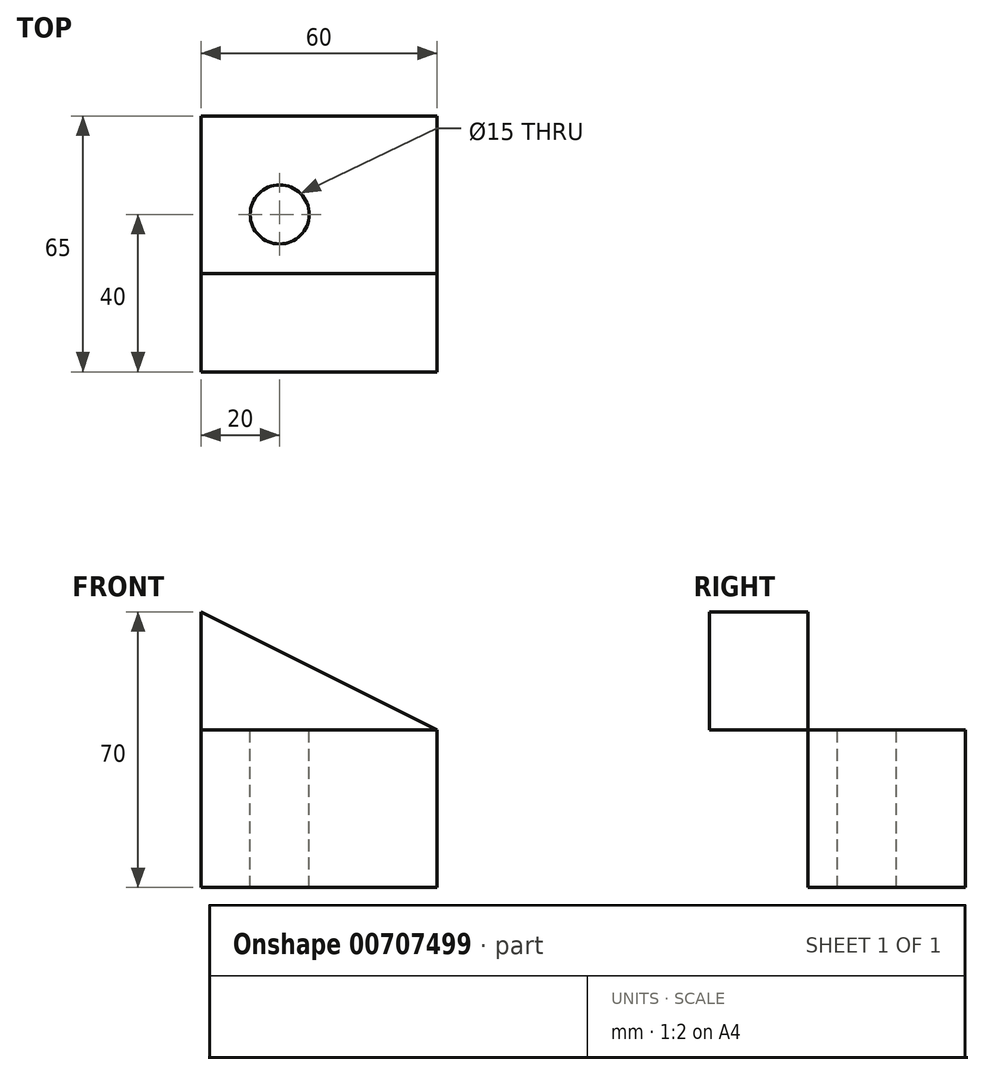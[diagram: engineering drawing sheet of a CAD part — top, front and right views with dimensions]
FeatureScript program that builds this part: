
annotation { "Feature Type Name" : "Feature", "Feature Type Description" : "" }
export const myFeature = defineFeature(function(context is Context, id is Id, definition is map)
    precondition{}
    {
        {
            var Q0;
            Q0=qCreatedBy(makeId("Front.planeOp"),FACE);
            var sketch = newSketch(context, id + "F0", { "sketchPlane" : qUnion([Q0])});
            skLineSegment(sketch, "E0.bottom", {"start": v(0, 0) * mm, "end": v(60, 0) * mm});
            skLineSegment(sketch, "E0.top", {"start": v(0, 40) * mm, "end": v(60, 40) * mm});
            skLineSegment(sketch, "E0.left", {"start": v(0, 0) * mm, "end": v(0, 40) * mm});
            skLineSegment(sketch, "E0.right", {"start": v(60, 0) * mm, "end": v(60, 40) * mm});
            skSolve(sketch);
        }
        {
            var Q0;
            Q0 = qSketchRegion(id + "F0", true);
            extrude(context, id + "F1", {"entities" : qUnion([Q0]), "depth" : 40 * mm, "offsetDistance" : 25 * mm});
        }
        {
            var Q0;
            Q0=makeQuery(id+"F1.opExtrude","SWEPT_FACE",FACE,{"disambiguationData":[OSD([sQuery(id+"F0.wireOp",EDGE,"E0.top")])]});
            var sketch = newSketch(context, id + "F2", { "sketchPlane" : qUnion([Q0])});
            skLineSegment(sketch, "E1", {"start": v(0, 0) * mm, "end": v(20, 0) * mm});
            skLineSegment(sketch, "E2", {"start": v(20, 0) * mm, "end": v(20, -25) * mm});
            skCircle(sketch, "E3", {"center": v(20, -25) * mm, "radius": 7.5 * mm});
            skSolve(sketch);
        }
        {
            var Q0;
            Q0=makeQuery(id+"F2.imprint","IMPRINT",FACE,{"disambiguationData":[TD([[makeQuery(id+"F2.imprint","IMPRINT",EDGE,{"derivedFrom":sQuery(id+"F2.wireOp",EDGE,"E3")}),1.0]])]});
            extrude(context, id + "F3", {"entities" : qUnion([Q0]), "operationType" : NewBodyOperationType.REMOVE, "endBound" : BoundingType.UP_TO_NEXT, "oppositeDirection" : true, "depth" : 25 * mm, "offsetDistance" : 25 * mm});
        }
        {
            var Q0;
            Q0=makeQuery(id+"F1.opExtrude","CAP_FACE",FACE,{"disambiguationData":[OSD([sQuery(id+"F0.wireOp",EDGE,"E0.bottom"),sQuery(id+"F0.wireOp",EDGE,"E0.top"),sQuery(id+"F0.wireOp",EDGE,"E0.left"),sQuery(id+"F0.wireOp",EDGE,"E0.right")])],"isStart":false});
            var sketch = newSketch(context, id + "F4", { "sketchPlane" : qUnion([Q0])});
            skLineSegment(sketch, "E4", {"start": v(0, 40) * mm, "end": v(0, 70) * mm});
            skLineSegment(sketch, "E5", {"start": v(0, 70) * mm, "end": v(60, 40) * mm});
            skSolve(sketch);
        }
        {
            var Q0;
            Q0=makeQuery(id+"F4.imprint","IMPRINT",FACE,{"disambiguationData":[TD([[makeQuery(id+"F4.imprint","IMPRINT",EDGE,{"derivedFrom":sQuery(id+"F4.wireOp",EDGE,"E4")}),-1.0]])]});
            extrude(context, id + "F5", {"entities" : qUnion([Q0]), "depth" : 25 * mm, "offsetDistance" : 25 * mm});
        }
    });
